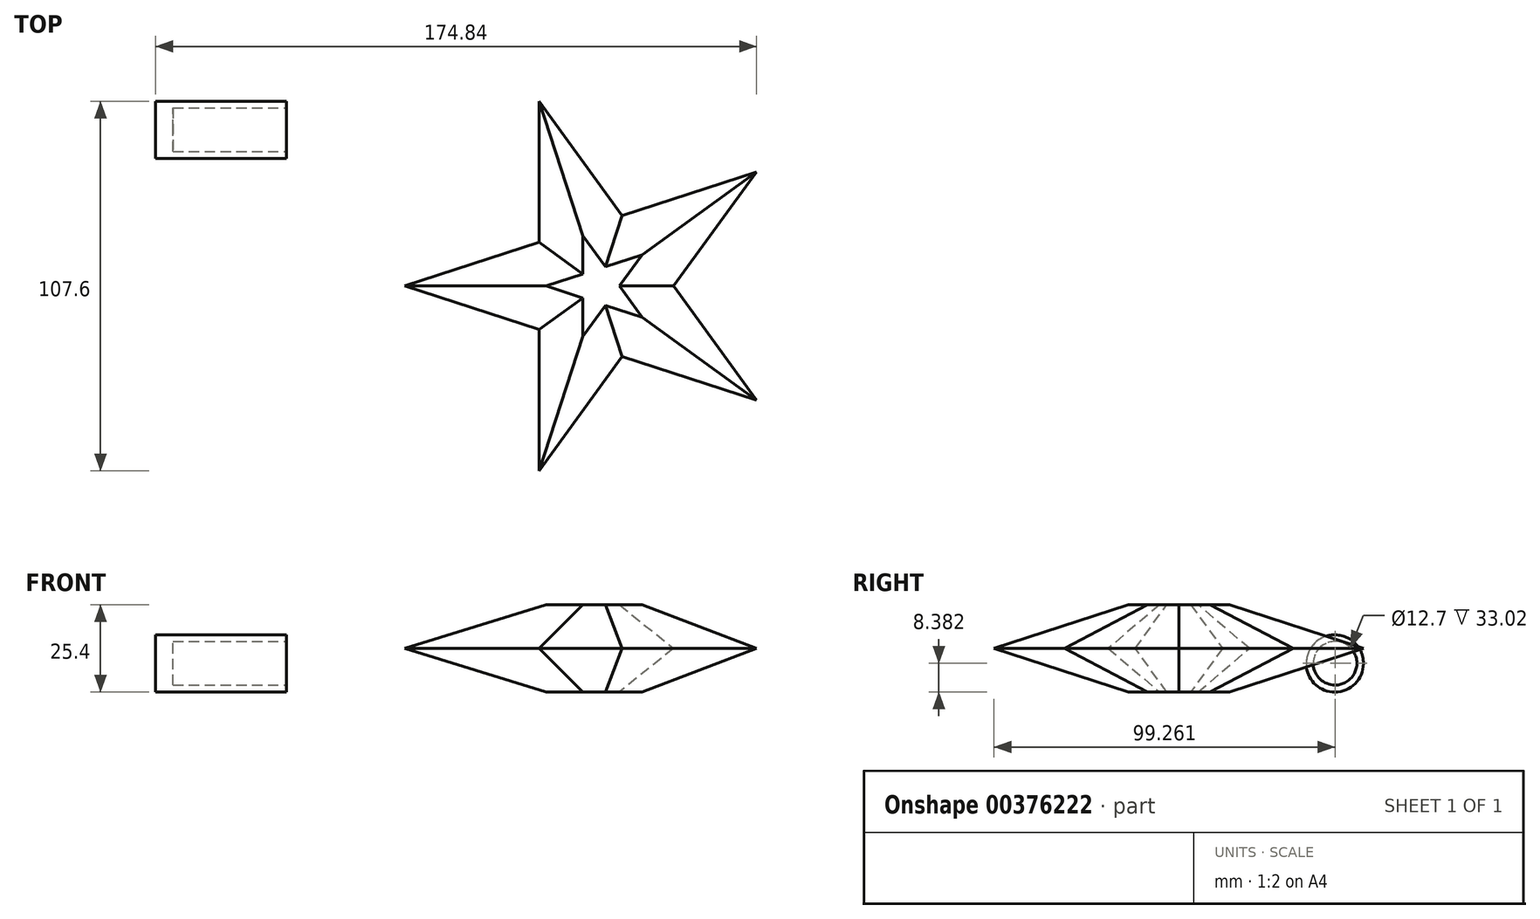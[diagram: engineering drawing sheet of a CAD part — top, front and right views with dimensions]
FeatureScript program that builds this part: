
annotation { "Feature Type Name" : "Feature", "Feature Type Description" : "" }
export const myFeature = defineFeature(function(context is Context, id is Id, definition is map)
    precondition{}
    {
        {
            var Q0;
            Q0=qCreatedBy(makeId("Top.planeOp"),FACE);
            var sketch = newSketch(context, id + "F0", { "sketchPlane" : qUnion([Q0])});
            skPoint(sketch, "E0.0.midPoint", {"position": v(-17.48, 0) * mm});
            skLineSegment(sketch, "E1", {"start": v(6.68, 20.55) * mm, "end": v(-17.48, 53.8) * mm});
            skLineSegment(sketch, "E2", {"start": v(-17.48, 12.7) * mm, "end": v(-17.48, 53.8) * mm});
            skLineSegment(sketch, "E3", {"start": v(-17.48, 53.8) * mm, "end": v(-17.48, 12.7) * mm});
            skLineSegment(sketch, "E4", {"start": v(6.68, -20.55) * mm, "end": v(-17.48, -53.8) * mm});
            skLineSegment(sketch, "E5", {"start": v(-17.48, -53.8) * mm, "end": v(-17.48, -12.7) * mm});
            skLineSegment(sketch, "E6", {"start": v(-17.48, -12.7) * mm, "end": v(-56.57, 0) * mm});
            skLineSegment(sketch, "E7", {"start": v(6.68, -20.55) * mm, "end": v(45.76, -33.25) * mm});
            skLineSegment(sketch, "E8", {"start": v(45.76, -33.25) * mm, "end": v(27.65, -8.31) * mm});
            skLineSegment(sketch, "E9", {"start": v(27.65, 8.31) * mm, "end": v(45.76, 33.25) * mm});
            skLineSegment(sketch, "E10", {"start": v(45.76, 33.25) * mm, "end": v(27.65, 8.31) * mm});
            skLineSegment(sketch, "E11.trimOffspring", {"start": v(27.65, -8.31) * mm, "end": v(45.76, -33.25) * mm});
            skLineSegment(sketch, "E12.trimOffspring", {"start": v(-17.48, 12.7) * mm, "end": v(-56.57, 0) * mm});
            skPoint(sketch, "E0.cCircle.center.orphan", {"position": v(0, 0) * mm});
            skLineSegment(sketch, "E13", {"start": v(-5.4, -37.17) * mm, "end": v(6.68, -20.55) * mm});
            skLineSegment(sketch, "E14", {"start": v(26.22, -26.9) * mm, "end": v(6.68, -20.55) * mm});
            skLineSegment(sketch, "E15", {"start": v(45.76, 33.25) * mm, "end": v(6.68, 20.55) * mm});
            skPoint(sketch, "E16.start.orphan", {"position": v(16.45, -23.72) * mm});
            skPoint(sketch, "E17.start.orphan", {"position": v(0.64, -28.86) * mm});
            skLineSegment(sketch, "E18", {"start": v(33.68, -16.62) * mm, "end": v(27.65, -8.31) * mm});
            skLineSegment(sketch, "E19", {"start": v(33.68, 16.62) * mm, "end": v(27.65, 8.31) * mm});
            skPoint(sketch, "E20.start.orphan", {"position": v(27.65, -8.31) * mm});
            skPoint(sketch, "E21.start.orphan", {"position": v(27.65, 8.31) * mm});
            skPoint(sketch, "E22.orphan", {"position": v(21.6, 0) * mm});
            skLineSegment(sketch, "E23", {"start": v(27.65, -8.31) * mm, "end": v(21.6, 0) * mm});
            skLineSegment(sketch, "E24", {"start": v(27.65, 8.31) * mm, "end": v(21.6, 0) * mm});
            skSolve(sketch);
        }
        {
            var Q0;
            {var subQ0=sQuery(id+"F0.wireOp",EDGE,"E1");Q0=makeQuery(id+"F0.imprint","IMPRINT",FACE,{"disambiguationData":[TD([[makeQuery(id+"F0.imprint","IMPRINT",EDGE,{"derivedFrom":subQ0}),1.0]])]});}
            extrude(context, id + "F1", {"entities" : qUnion([Q0]), "depth" : 25.4 * mm});
        }
        {
            var Q0;
            Q0=makeQuery(id+"F1.opExtrude","CAP_FACE",FACE,{"disambiguationData":[OSD([sQuery(id+"F0.wireOp",EDGE,"E1"),sQuery(id+"F0.wireOp",EDGE,"E3"),sQuery(id+"F0.wireOp",EDGE,"E4"),sQuery(id+"F0.wireOp",EDGE,"E5"),sQuery(id+"F0.wireOp",EDGE,"E6"),sQuery(id+"F0.wireOp",EDGE,"E7"),sQuery(id+"F0.wireOp",EDGE,"E10"),sQuery(id+"F0.wireOp",EDGE,"E11.trimOffspring"),sQuery(id+"F0.wireOp",EDGE,"E12.trimOffspring"),sQuery(id+"F0.wireOp",EDGE,"E13"),sQuery(id+"F0.wireOp",EDGE,"E14"),sQuery(id+"F0.wireOp",EDGE,"E15"),sQuery(id+"F0.wireOp",EDGE,"E18"),sQuery(id+"F0.wireOp",EDGE,"E19"),sQuery(id+"F0.wireOp",EDGE,"E23"),sQuery(id+"F0.wireOp",EDGE,"E24")])],"isStart":true});
            var Q1;
            Q1=makeQuery(id+"F1.opExtrude","CAP_FACE",FACE,{"disambiguationData":[OSD([sQuery(id+"F0.wireOp",EDGE,"E1"),sQuery(id+"F0.wireOp",EDGE,"E3"),sQuery(id+"F0.wireOp",EDGE,"E4"),sQuery(id+"F0.wireOp",EDGE,"E5"),sQuery(id+"F0.wireOp",EDGE,"E6"),sQuery(id+"F0.wireOp",EDGE,"E7"),sQuery(id+"F0.wireOp",EDGE,"E10"),sQuery(id+"F0.wireOp",EDGE,"E11.trimOffspring"),sQuery(id+"F0.wireOp",EDGE,"E12.trimOffspring"),sQuery(id+"F0.wireOp",EDGE,"E13"),sQuery(id+"F0.wireOp",EDGE,"E14"),sQuery(id+"F0.wireOp",EDGE,"E15"),sQuery(id+"F0.wireOp",EDGE,"E18"),sQuery(id+"F0.wireOp",EDGE,"E19"),sQuery(id+"F0.wireOp",EDGE,"E23"),sQuery(id+"F0.wireOp",EDGE,"E24")])],"isStart":false});
            chamfer(context, id + "F2", {"entities" : qUnion([Q0, Q1]), "width" : 12.7 * mm, "tangentPropagation" : true});
        }
        {
            var Q0;
            Q0=qCreatedBy(makeId("Top.planeOp"),FACE);
            var sketch = newSketch(context, id + "F3", { "sketchPlane" : qUnion([Q0])});
            skLineSegment(sketch, "E25.bottom", {"start": v(-90.98, 53.72) * mm, "end": v(-129.08, 53.72) * mm});
            skLineSegment(sketch, "E25.top", {"start": v(-90.98, 37.08) * mm, "end": v(-129.08, 37.08) * mm});
            skLineSegment(sketch, "E25.left", {"start": v(-90.98, 53.72) * mm, "end": v(-90.98, 37.08) * mm});
            skLineSegment(sketch, "E25.right", {"start": v(-129.08, 53.72) * mm, "end": v(-129.08, 37.08) * mm});
            skSolve(sketch);
        }
        {
            var Q0;
            Q0=makeQuery(id+"F3.imprint","IMPRINT",FACE,{"disambiguationData":[TD([[makeQuery(id+"F3.imprint","IMPRINT",EDGE,{"derivedFrom":sQuery(id+"F3.wireOp",EDGE,"E25.bottom")}),1.0]])]});
            extrude(context, id + "F4", {"entities" : qUnion([Q0]), "depth" : 16.64 * mm});
        }
        {
            var Q0;
            Q0=makeQuery(id+"F4.opExtrude","CAP_EDGE",EDGE,{"disambiguationData":[OSD([sQuery(id+"F3.wireOp",EDGE,"E25.bottom")])],"isStart":false});
            var Q1;
            Q1=makeQuery(id+"F4.opExtrude","CAP_EDGE",EDGE,{"disambiguationData":[OSD([sQuery(id+"F3.wireOp",EDGE,"E25.top")])],"isStart":false});
            var Q2;
            Q2=makeQuery(id+"F4.opExtrude","CAP_EDGE",EDGE,{"disambiguationData":[OSD([sQuery(id+"F3.wireOp",EDGE,"E25.bottom")])],"isStart":true});
            var Q3;
            Q3=makeQuery(id+"F4.opExtrude","CAP_EDGE",EDGE,{"disambiguationData":[OSD([sQuery(id+"F3.wireOp",EDGE,"E25.top")])],"isStart":true});
            fillet(context, id + "F5", {"entities" : qUnion([Q0, Q1, Q2, Q3]), "radius" : 8.25 * mm, "tangentPropagation" : true, "allowEdgeOverflow" : false});
        }
        {
            var Q0;
            Q0=makeQuery(id+"F4.opExtrude","SWEPT_FACE",FACE,{"disambiguationData":[OSD([sQuery(id+"F3.wireOp",EDGE,"E25.left")])]});
            var sketch = newSketch(context, id + "F6", { "sketchPlane" : qUnion([Q0])});
            skCircle(sketch, "E26", {"center": v(45.46, 8.38) * mm, "radius": 6.35 * mm});
            skSolve(sketch);
        }
        {
            var Q0;
            Q0=makeQuery(id+"F6.imprint","IMPRINT",FACE,{"disambiguationData":[TD([[makeQuery(id+"F6.imprint","IMPRINT",EDGE,{"derivedFrom":sQuery(id+"F6.wireOp",EDGE,"E26")}),1.0]])]});
            extrude(context, id + "F7", {"entities" : qUnion([Q0]), "operationType" : NewBodyOperationType.REMOVE, "oppositeDirection" : true, "depth" : 33.02 * mm});
        }
    });
